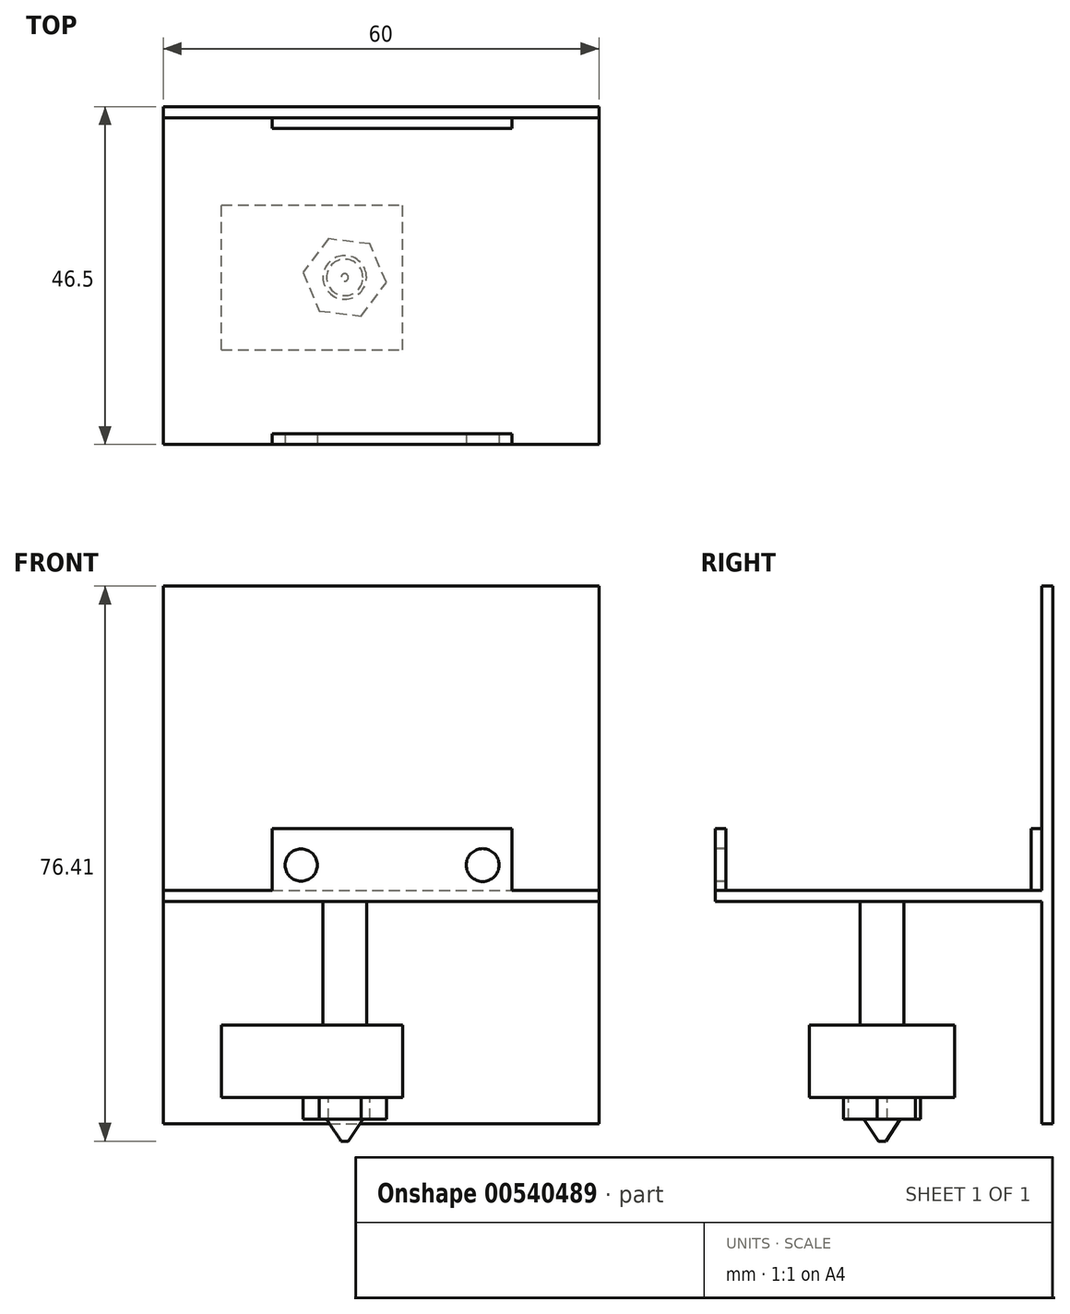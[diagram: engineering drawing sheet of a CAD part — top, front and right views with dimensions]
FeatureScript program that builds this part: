
annotation { "Feature Type Name" : "Feature", "Feature Type Description" : "" }
export const myFeature = defineFeature(function(context is Context, id is Id, definition is map)
    precondition{}
    {
        {
            var Q0;
            Q0=qCreatedBy(makeId("Front.planeOp"),FACE);
            var sketch = newSketch(context, id + "F0", { "sketchPlane" : qUnion([Q0])});
            skLineSegment(sketch, "E0.bottom", {"start": v(-30.6, 54) * mm, "end": v(29.4, 54) * mm});
            skLineSegment(sketch, "E0.top", {"start": v(-30.6, -20) * mm, "end": v(29.4, -20) * mm});
            skLineSegment(sketch, "E0.left", {"start": v(-30.6, 54) * mm, "end": v(-30.6, -20) * mm});
            skLineSegment(sketch, "E0.right", {"start": v(29.4, 54) * mm, "end": v(29.4, -20) * mm});
            skSolve(sketch);
        }
        {
            var Q0;
            Q0=makeQuery(id+"F0.imprint","IMPRINT",FACE,{"disambiguationData":[TD([[makeQuery(id+"F0.imprint","IMPRINT",EDGE,{"derivedFrom":sQuery(id+"F0.wireOp",EDGE,"E0.bottom")}),-1.0]])]});
            extrude(context, id + "F1", {"entities" : qUnion([Q0]), "depth" : 1.5 * mm, "offsetDistance" : 25 * mm});
        }
        {
            var Q0;
            Q0=makeQuery(id+"F1.opExtrude","CAP_FACE",FACE,{"disambiguationData":[OSD([sQuery(id+"F0.wireOp",EDGE,"E0.bottom"),sQuery(id+"F0.wireOp",EDGE,"E0.top"),sQuery(id+"F0.wireOp",EDGE,"E0.left"),sQuery(id+"F0.wireOp",EDGE,"E0.right")])],"isStart":false});
            var sketch = newSketch(context, id + "F2", { "sketchPlane" : qUnion([Q0])});
            skLineSegment(sketch, "E1.bottom", {"start": v(-15.6, 20.6) * mm, "end": v(17.4, 20.6) * mm});
            skLineSegment(sketch, "E1.top", {"start": v(-15.6, 10.6) * mm, "end": v(17.4, 10.6) * mm});
            skLineSegment(sketch, "E1.left", {"start": v(-15.6, 20.6) * mm, "end": v(-15.6, 10.6) * mm});
            skLineSegment(sketch, "E1.right", {"start": v(17.4, 20.6) * mm, "end": v(17.4, 10.6) * mm});
            skSolve(sketch);
        }
        {
            var Q0;
            Q0=makeQuery(id+"F2.imprint","IMPRINT",FACE,{"disambiguationData":[TD([[makeQuery(id+"F2.imprint","IMPRINT",EDGE,{"derivedFrom":sQuery(id+"F2.wireOp",EDGE,"E1.bottom")}),-1.0]])]});
            extrude(context, id + "F3", {"entities" : qUnion([Q0]), "depth" : 1.5 * mm, "offsetDistance" : 25 * mm});
        }
        {
            var Q0;
            Q0=makeQuery(id+"F3.opExtrude","SWEPT_FACE",FACE,{"disambiguationData":[OSD([sQuery(id+"F2.wireOp",EDGE,"E1.top")])]});
            var sketch = newSketch(context, id + "F4", { "sketchPlane" : qUnion([Q0])});
            skLineSegment(sketch, "E2.bottom", {"start": v(-30.6, 1.5) * mm, "end": v(29.4, 1.5) * mm});
            skLineSegment(sketch, "E2.top", {"start": v(-30.6, 46.5) * mm, "end": v(29.4, 46.5) * mm});
            skLineSegment(sketch, "E2.left", {"start": v(-30.6, 1.5) * mm, "end": v(-30.6, 46.5) * mm});
            skLineSegment(sketch, "E2.right", {"start": v(29.4, 1.5) * mm, "end": v(29.4, 46.5) * mm});
            skSolve(sketch);
        }
        {
            var Q0;
            Q0=makeQuery(id+"F4.imprint","IMPRINT",FACE,{"disambiguationData":[TD([[makeQuery(id+"F4.imprint","IMPRINT",EDGE,{"derivedFrom":sQuery(id+"F4.wireOp",EDGE,"E2.top")}),-1.0]])]});
            extrude(context, id + "F5", {"entities" : qUnion([Q0]), "operationType" : NewBodyOperationType.ADD, "oppositeDirection" : true, "depth" : 1.5 * mm, "offsetDistance" : 25 * mm});
        }
        {
            var Q0;
            Q0=makeQuery(id+"F5.opExtrude","SWEPT_FACE",FACE,{"disambiguationData":[OSD([sQuery(id+"F4.wireOp",EDGE,"E2.top")])]});
            var sketch = newSketch(context, id + "F6", { "sketchPlane" : qUnion([Q0])});
            skLineSegment(sketch, "E3.0.0", {"start": v(-15.6, 20.6) * mm, "end": v(-15.6, 12.1) * mm});
            skLineSegment(sketch, "E3.0.2", {"start": v(17.4, 12.1) * mm, "end": v(17.4, 20.6) * mm});
            skLineSegment(sketch, "E3.0.3", {"start": v(17.4, 20.6) * mm, "end": v(-15.6, 20.6) * mm});
            skLineSegment(sketch, "E4.top", {"start": v(-15.6, 10.6) * mm, "end": v(17.4, 10.6) * mm});
            skLineSegment(sketch, "E4.left", {"start": v(-15.6, 12.1) * mm, "end": v(-15.6, 10.6) * mm});
            skLineSegment(sketch, "E4.right", {"start": v(17.4, 12.1) * mm, "end": v(17.4, 10.6) * mm});
            skSolve(sketch);
        }
        {
            var Q0;
            {var subQ0=sQuery(id+"F6.wireOp",EDGE,"E3.0.0");Q0=makeQuery(id+"F6.imprint","IMPRINT",FACE,{"disambiguationData":[TD([[makeQuery(id+"F6.imprint","IMPRINT",EDGE,{"derivedFrom":subQ0}),1.0]])]});}
            var Q1;
            Q1=makeQuery(id+"F6.imprint","IMPRINT",FACE,{"disambiguationData":[TD([[makeQuery(id+"F6.imprint","IMPRINT",EDGE,{"derivedFrom":sQuery(id+"F6.wireOp",EDGE,"E4.top")}),1.0]])]});
            extrude(context, id + "F7", {"entities" : qUnion([Q0, Q1]), "operationType" : NewBodyOperationType.ADD, "oppositeDirection" : true, "depth" : 1.5 * mm, "offsetDistance" : 25 * mm});
        }
        {
            var Q0;
            Q0=makeQuery(id+"F7.boolean.opBoolean","MERGE",FACE,{"derivedFrom":[makeQuery(id+"F5.opExtrude","SWEPT_FACE",FACE,{"disambiguationData":[OSD([sQuery(id+"F4.wireOp",EDGE,"E2.top")])]}),makeQuery(id+"F7.opExtrude","CAP_FACE",FACE,{"disambiguationData":[OSD([sQuery(id+"F6.wireOp",EDGE,"E3.0.0"),sQuery(id+"F6.wireOp",EDGE,"E3.0.2"),sQuery(id+"F6.wireOp",EDGE,"E3.0.3"),sQuery(id+"F6.wireOp",EDGE,"E4.top"),sQuery(id+"F6.wireOp",EDGE,"E4.left"),sQuery(id+"F6.wireOp",EDGE,"E4.right")])],"isStart":true})]});
            var sketch = newSketch(context, id + "F8", { "sketchPlane" : qUnion([Q0])});
            skLineSegment(sketch, "E5", {"start": v(-43.89, 15.6) * mm, "end": v(56.64, 15.6) * mm, "construction": true});
            skCircle(sketch, "E6", {"center": v(-11.6, 15.6) * mm, "radius": 2.22 * mm});
            skCircle(sketch, "E7", {"center": v(13.4, 15.6) * mm, "radius": 2.26 * mm});
            skSolve(sketch);
        }
        {
            var Q0;
            Q0=qSketchRegion(id+"F8",true);
            extrude(context, id + "F9", {"entities" : qUnion([Q0]), "operationType" : NewBodyOperationType.REMOVE, "endBound" : BoundingType.SYMMETRIC, "oppositeDirection" : true, "depth" : 5 * mm, "offsetDistance" : 25 * mm});
        }
        {
            var Q0;
            {var subQ0=sQuery(id+"F2.wireOp",EDGE,"E1.top");Q0=makeQuery(id+"F5.boolean.opBoolean","MERGE",FACE,{"derivedFrom":[makeQuery(id+"F3.opExtrude","SWEPT_FACE",FACE,{"disambiguationData":[OSD([subQ0])]}),makeQuery(id+"F5.opExtrude","CAP_FACE",FACE,{"disambiguationData":[OSD([subQ0,sQuery(id+"F2.wireOp",EDGE,"E1.left"),sQuery(id+"F2.wireOp",EDGE,"E1.right"),sQuery(id+"F4.wireOp",EDGE,"E2.bottom"),sQuery(id+"F4.wireOp",EDGE,"E2.top"),sQuery(id+"F4.wireOp",EDGE,"E2.left"),sQuery(id+"F4.wireOp",EDGE,"E2.right")])],"isStart":true})]});}
            var sketch = newSketch(context, id + "F10", { "sketchPlane" : qUnion([Q0])});
            skCircle(sketch, "E8", {"center": v(-5.6, 23.5) * mm, "radius": 3 * mm});
            skSolve(sketch);
        }
        {
            var Q0;
            Q0=qSketchRegion(id+"F10",true);
            extrude(context, id + "F11", {"entities" : qUnion([Q0]), "depth" : 17 * mm, "offsetDistance" : 25 * mm});
        }
        {
            var Q0;
            Q0=makeQuery(id+"F11.opExtrude","CAP_FACE",FACE,{"disambiguationData":[OSD([sQuery(id+"F10.wireOp",EDGE,"E8")])],"isStart":false});
            var sketch = newSketch(context, id + "F12", { "sketchPlane" : qUnion([Q0])});
            skCircle(sketch, "E9.0.0", {"center": v(-5.6, 23.5) * mm, "radius": 3 * mm});
            skLineSegment(sketch, "E10.bottom", {"start": v(-22.6, 33.5) * mm, "end": v(2.4, 33.5) * mm});
            skLineSegment(sketch, "E10.top", {"start": v(-22.6, 13.5) * mm, "end": v(2.4, 13.5) * mm});
            skLineSegment(sketch, "E10.left", {"start": v(-22.6, 33.5) * mm, "end": v(-22.6, 13.5) * mm});
            skLineSegment(sketch, "E10.right", {"start": v(2.4, 33.5) * mm, "end": v(2.4, 13.5) * mm});
            skSolve(sketch);
        }
        {
            var Q0;
            Q0=qSketchRegion(id+"F12",true);
            var Q1;
            Q1=makeQuery(id+"F12.imprint","IMPRINT",FACE,{"disambiguationData":[TD([[makeQuery(id+"F12.imprint","IMPRINT",EDGE,{"derivedFrom":sQuery(id+"F12.wireOp",EDGE,"E9.0.0")}),1.0]])]});
            extrude(context, id + "F13", {"entities" : qUnion([Q0, Q1]), "operationType" : NewBodyOperationType.ADD, "depth" : 10 * mm, "offsetDistance" : 25 * mm});
        }
        {
            var Q0;
            Q0=makeQuery(id+"F13.opExtrude","CAP_FACE",FACE,{"disambiguationData":[OSD([sQuery(id+"F12.wireOp",EDGE,"E9.0.0"),sQuery(id+"F12.wireOp",EDGE,"E10.bottom"),sQuery(id+"F12.wireOp",EDGE,"E10.top"),sQuery(id+"F12.wireOp",EDGE,"E10.left"),sQuery(id+"F12.wireOp",EDGE,"E10.right")])],"isStart":false});
            var sketch = newSketch(context, id + "F14", { "sketchPlane" : qUnion([Q0])});
            skCircle(sketch, "E11.cCircle", {"center": v(-5.6, 23.5) * mm, "radius": 5 * mm, "construction": true});
            skLineSegment(sketch, "E11.0", {"start": v(-3.36, 28.82) * mm, "end": v(0.13, 24.21) * mm});
            skLineSegment(sketch, "E11.1", {"start": v(0.13, 24.21) * mm, "end": v(-2.12, 18.9) * mm});
            skLineSegment(sketch, "E11.2", {"start": v(-2.12, 18.9) * mm, "end": v(-7.85, 18.18) * mm});
            skLineSegment(sketch, "E11.3", {"start": v(-7.85, 18.18) * mm, "end": v(-11.33, 22.79) * mm});
            skLineSegment(sketch, "E11.4", {"start": v(-11.33, 22.79) * mm, "end": v(-9.09, 28.1) * mm});
            skLineSegment(sketch, "E11.5", {"start": v(-9.09, 28.1) * mm, "end": v(-3.36, 28.82) * mm});
            skPoint(sketch, "E11.0.midPoint", {"position": v(-1.62, 26.52) * mm});
            skSolve(sketch);
        }
        {
            var Q0;
            Q0=makeQuery(id+"F14.imprint","IMPRINT",FACE,{"disambiguationData":[TD([[makeQuery(id+"F14.imprint","IMPRINT",EDGE,{"derivedFrom":sQuery(id+"F14.wireOp",EDGE,"E11.0")}),-1.0]])]});
            var Q1;
            Q1=makeQuery(id+"F14.imprint","IMPRINT",FACE,{"disambiguationData":[TD([[makeQuery(id+"F14.imprint","IMPRINT",EDGE,{"derivedFrom":makeQuery(id+"F13.opExtrude","CAP_EDGE",EDGE,{"disambiguationData":[OSD([sQuery(id+"F12.wireOp",EDGE,"E9.0.0")])],"isStart":false})}),1.0]])]});
            extrude(context, id + "F15", {"entities" : qUnion([Q0, Q1]), "depth" : 3 * mm, "offsetDistance" : 25 * mm});
        }
        {
            var Q0;
            Q0=makeQuery(id+"F15.opExtrude","CAP_FACE",FACE,{"disambiguationData":[OSD([sQuery(id+"F14.wireOp",EDGE,"E11.0"),sQuery(id+"F14.wireOp",EDGE,"E11.1"),sQuery(id+"F14.wireOp",EDGE,"E11.2"),sQuery(id+"F14.wireOp",EDGE,"E11.3"),sQuery(id+"F14.wireOp",EDGE,"E11.4"),sQuery(id+"F14.wireOp",EDGE,"E11.5")])],"isStart":false});
            var sketch = newSketch(context, id + "F16", { "sketchPlane" : qUnion([Q0])});
            skCircle(sketch, "E12.0", {"center": v(-5.6, 23.5) * mm, "radius": 3 * mm});
            skCircle(sketch, "E13", {"center": v(-5.6, 23.5) * mm, "radius": 2.5 * mm});
            skSolve(sketch);
        }
        {
            var Q0;
            Q0=makeQuery(id+"F16.imprint","IMPRINT",FACE,{"disambiguationData":[TD([[makeQuery(id+"F16.imprint","IMPRINT",EDGE,{"derivedFrom":sQuery(id+"F16.wireOp",EDGE,"E13")}),1.0]])]});
            extrude(context, id + "F17", {"entities" : qUnion([Q0]), "operationType" : NewBodyOperationType.ADD, "depth" : 3 * mm, "offsetDistance" : 25 * mm});
        }
        {
            var Q0;
            Q0=makeQuery(id+"F17.opExtrude","CAP_EDGE",EDGE,{"disambiguationData":[OSD([sQuery(id+"F16.wireOp",EDGE,"E13")])],"isStart":false});
            chamfer(context, id + "F18", {"entities" : qUnion([Q0]), "chamferType" : ChamferType.TWO_OFFSETS, "width1" : 2 * mm, "oppositeDirection" : false, "width2" : 3 * mm, "tangentPropagation" : true});
        }
    });
